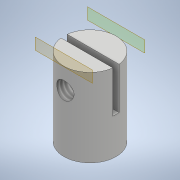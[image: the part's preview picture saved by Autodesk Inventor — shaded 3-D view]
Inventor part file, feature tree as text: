
AUTODESK INVENTOR PART (.ipt)
format: ipt  version: 2021 (Build 250183000, 183)  size: 150,016 bytes
history: native  units: mm
features: sketch x6, extrude x4, hole x2, plane x2
ambient origin geometry x8: Origin, YZ Plane, XZ Plane, XY Plane, X Axis, Y Axis, Z Axis, Center Point
bodies: Solid1 (feature_tree)
feature tree (14):
  extrude  "Extrusion1"  Depth=15.0mm TaperAngle=0.0deg
  sketch  "Sketch2"  dims[d3=1.0mm]
  hole  "Hole1"  [1 undecoded]
  extrude  "Extrusion2"  Depth=4.5mm
  plane  "Work Plane1"
  plane  "Work Plane2"
  hole  "Hole2"  [1 undecoded]
  extrude  "Extrusion3"  Depth=10.0mm TaperAngle=0.0deg
  extrude  "Extrusion4"  Depth=1.2mm
  sketch  "Sketch1"  dims[d0=10.0mm d1=15.0mm d2=0.0mm]
  sketch  "Sketch3"  dims[d4=3.302mm d5=5.0mm d6=4.0mm d7=2.0mm d8=90.0deg d9=7.0mm d10=0.0mm d11=2.0mm d12=0.0mm]
  sketch  "Sketch5"  dims[d13=4.5mm d15=4.5mm]
  sketch  "Sketch6"  dims[d16=4.0mm]
  sketch  "Sketch7"  dims[d17=3.302mm d18=4.5mm d19=4.0mm d20=2.0mm d21=90.0deg d22=4.5mm d23=0.0mm d31=2.0mm d32=0.0mm d33=10.0mm d34=0.0mm d35=1.2mm d36=0.6mm d37=1.0mm d38=1.0mm]
note: 2 required parameter values undecoded (feature->parameter linkage not recoverable at this tier; creation-order binding heuristic only, values carry confidence <= 0.55)
